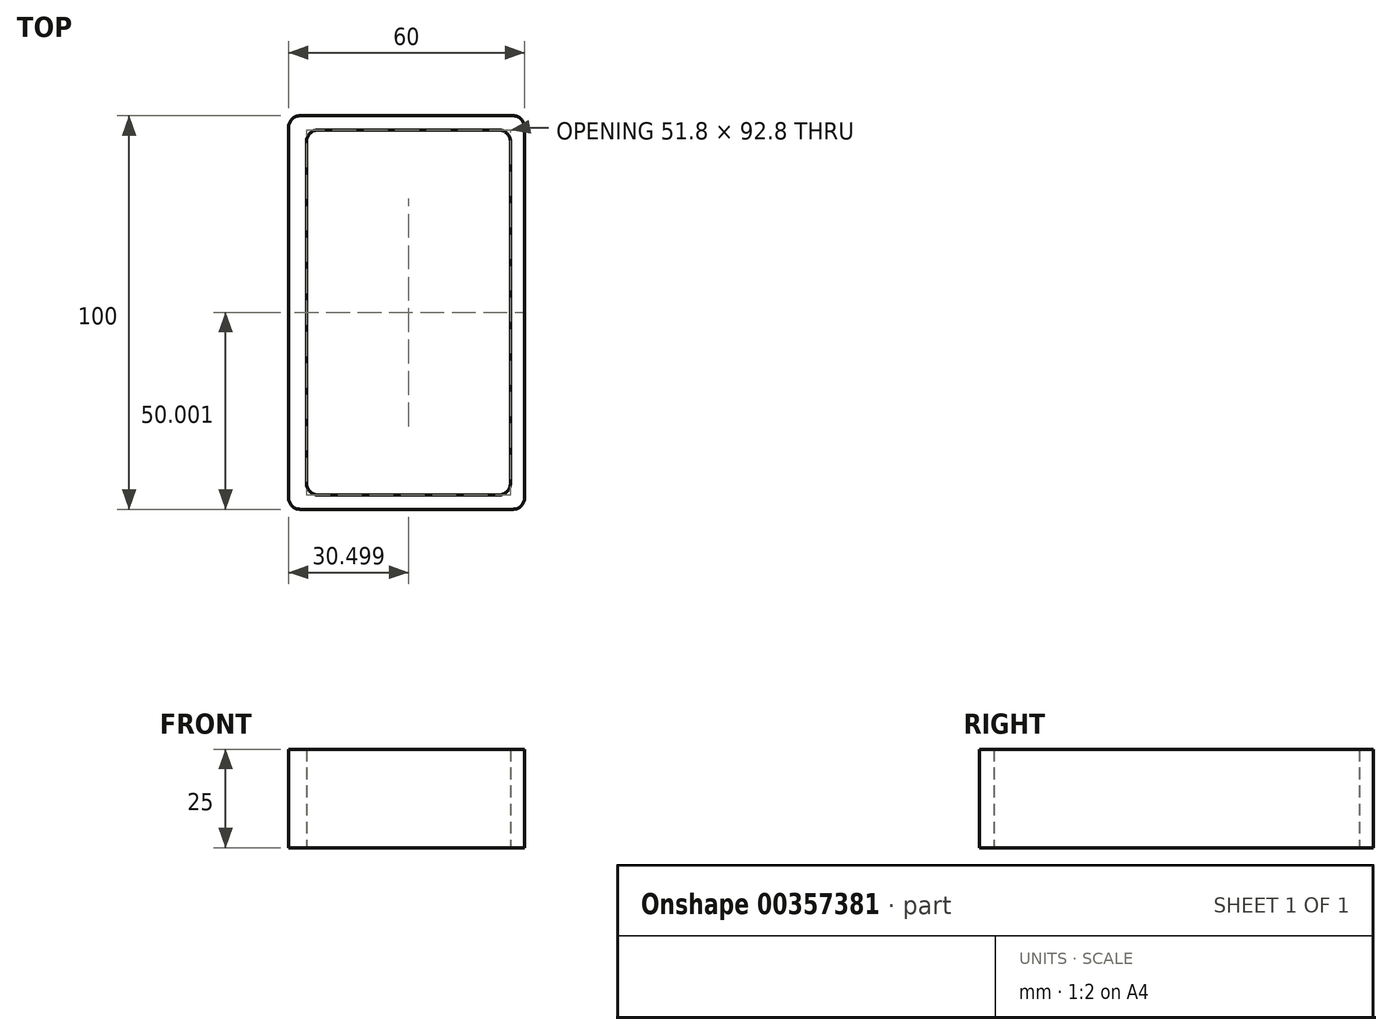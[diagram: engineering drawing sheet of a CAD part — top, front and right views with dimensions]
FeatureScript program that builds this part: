
annotation { "Feature Type Name" : "Feature", "Feature Type Description" : "" }
export const myFeature = defineFeature(function(context is Context, id is Id, definition is map)
    precondition{}
    {
        {
            var Q0;
            Q0=qCreatedBy(makeId("Top.planeOp"),FACE);
            var sketch = newSketch(context, id + "F0", { "sketchPlane" : qUnion([Q0])});
            skLineSegment(sketch, "E0", {"start": v(39.6, 32.04) * mm, "end": v(39.6, -61.96) * mm});
            skLineSegment(sketch, "E1", {"start": v(36.6, 35.04) * mm, "end": v(-17.4, 35.04) * mm});
            skLineSegment(sketch, "E2", {"start": v(-20.4, 32.04) * mm, "end": v(-20.4, -61.96) * mm});
            skLineSegment(sketch, "E3", {"start": v(-17.4, -64.96) * mm, "end": v(9.6, -64.96) * mm});
            skLineSegment(sketch, "E4", {"start": v(10.6, -61.36) * mm, "end": v(-12.8, -61.36) * mm});
            skLineSegment(sketch, "E5", {"start": v(-15.8, -58.36) * mm, "end": v(-15.8, 28.44) * mm});
            skPoint(sketch, "E6.start.orphan", {"position": v(9.6, -64.96) * mm});
            skPoint(sketch, "E7.end.orphan", {"position": v(37, -5.88) * mm});
            skPoint(sketch, "E8.end.orphan", {"position": v(10.6, 31.44) * mm});
            skPoint(sketch, "E8.start.orphan", {"position": v(9.6, 35.04) * mm});
            skPoint(sketch, "E9.end.orphan", {"position": v(-15.8, -22.5) * mm});
            skPoint(sketch, "E10.visualSharp", {"position": v(39.6, 35.04) * mm});
            skArc(sketch, "E10.filletArc", {"start": v(39.6, 32.04) * mm, "mid": v(38.72, 34.16) * mm, "end": v(36.6, 35.04) * mm});
            skPoint(sketch, "E11.visualSharp", {"position": v(37, 31.44) * mm});
            skPoint(sketch, "E12.visualSharp", {"position": v(39.6, -64.96) * mm});
            skPoint(sketch, "E13.visualSharp", {"position": v(-20.4, -64.96) * mm});
            skArc(sketch, "E13.filletArc", {"start": v(-20.4, -61.96) * mm, "mid": v(-19.52, -64.08) * mm, "end": v(-17.4, -64.96) * mm});
            skPoint(sketch, "E14.visualSharp", {"position": v(-15.8, -61.36) * mm});
            skArc(sketch, "E14.filletArc", {"start": v(-15.8, -58.36) * mm, "mid": v(-14.92, -60.48) * mm, "end": v(-12.8, -61.36) * mm});
            skPoint(sketch, "E15.visualSharp", {"position": v(-20.4, 35.04) * mm});
            skArc(sketch, "E15.filletArc", {"start": v(-17.4, 35.04) * mm, "mid": v(-19.52, 34.16) * mm, "end": v(-20.4, 32.04) * mm});
            skPoint(sketch, "E16.visualSharp", {"position": v(-15.8, 31.44) * mm});
            skArc(sketch, "E16.filletArc", {"start": v(-12.8, 31.44) * mm, "mid": v(-14.92, 30.56) * mm, "end": v(-15.8, 28.44) * mm});
            skLineSegment(sketch, "E17", {"start": v(9.6, 31.44) * mm, "end": v(10.6, 31.44) * mm});
            skLineSegment(sketch, "E18", {"start": v(-12.8, 31.44) * mm, "end": v(33, 31.44) * mm});
            skLineSegment(sketch, "E19", {"start": v(36, 28.44) * mm, "end": v(36, -58.36) * mm});
            skLineSegment(sketch, "E20", {"start": v(33, -61.36) * mm, "end": v(10.6, -61.36) * mm});
            skLineSegment(sketch, "E21", {"start": v(9.6, -64.96) * mm, "end": v(36.6, -64.96) * mm});
            skLineSegment(sketch, "E22", {"start": v(39.6, -61.96) * mm, "end": v(39.6, -61.96) * mm});
            skArc(sketch, "E23.filletArc", {"start": v(36.6, -64.96) * mm, "mid": v(38.72, -64.08) * mm, "end": v(39.6, -61.96) * mm});
            skPoint(sketch, "E24.visualSharp", {"position": v(36, -61.36) * mm});
            skArc(sketch, "E24.filletArc", {"start": v(33, -61.36) * mm, "mid": v(35.12, -60.48) * mm, "end": v(36, -58.36) * mm});
            skPoint(sketch, "E25.visualSharp", {"position": v(36, 31.44) * mm});
            skArc(sketch, "E25.filletArc", {"start": v(36, 28.44) * mm, "mid": v(35.12, 30.56) * mm, "end": v(33, 31.44) * mm});
            skPoint(sketch, "E26.end.orphan", {"position": v(36, -14.96) * mm});
            skPoint(sketch, "E26.start.orphan", {"position": v(39.6, -14.96) * mm});
            skSolve(sketch);
        }
        {
            var Q0;
            Q0=makeQuery(id+"F0.imprint","IMPRINT",FACE,{"disambiguationData":[TD([[makeQuery(id+"F0.imprint","IMPRINT",EDGE,{"derivedFrom":sQuery(id+"F0.wireOp",EDGE,"E0")}),-1.0]])]});
            extrude(context, id + "F1", {"entities" : qUnion([Q0]), "depth" : 25 * mm});
        }
    });
